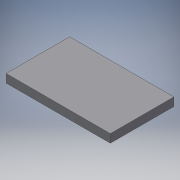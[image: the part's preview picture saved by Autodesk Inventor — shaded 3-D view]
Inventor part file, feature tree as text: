
AUTODESK INVENTOR PART (.ipt)
format: ipt  version: 2018 (Build 220112000, 112)  size: 90,112 bytes
history: native  units: mm
features: extrude x1, sketch x1
ambient origin geometry x8: Origin, YZ Plane, XZ Plane, XY Plane, X Axis, Y Axis, Z Axis, Center Point
bodies: Solido1 (feature_tree)
feature tree (2):
  extrude  "Estrusione1"  Depth=100.0mm
  sketch  "Schizzo1"
